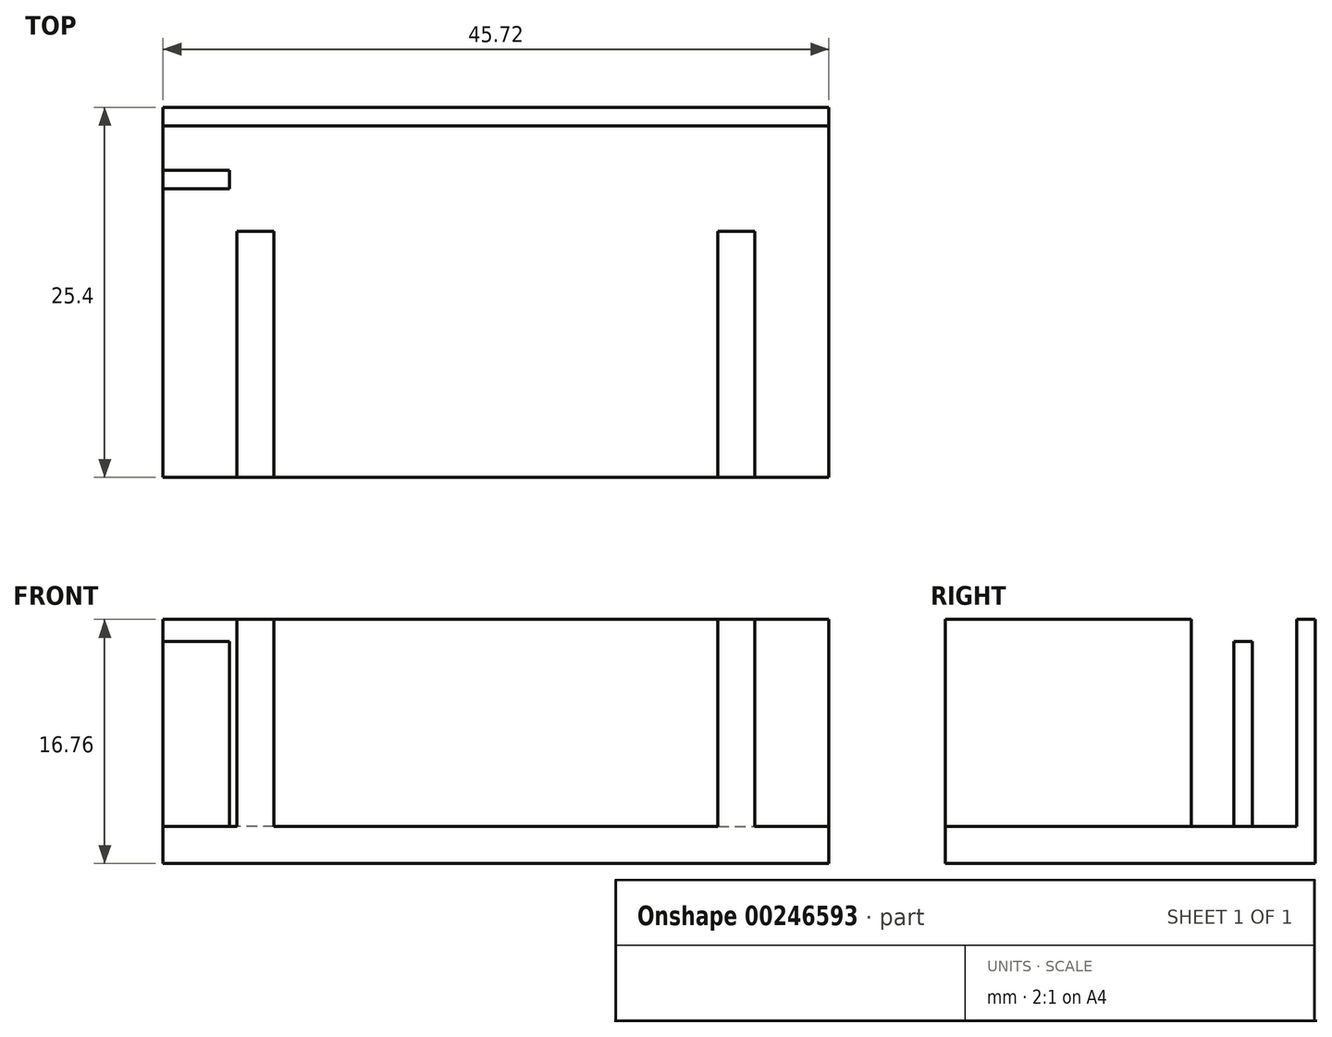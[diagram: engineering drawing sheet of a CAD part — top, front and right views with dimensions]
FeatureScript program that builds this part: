
annotation { "Feature Type Name" : "Feature", "Feature Type Description" : "" }
export const myFeature = defineFeature(function(context is Context, id is Id, definition is map)
    precondition{}
    {
        {
            var Q0;
            Q0=qCreatedBy(makeId("Top.planeOp"),FACE);
            var sketch = newSketch(context, id + "F0", { "sketchPlane" : qUnion([Q0])});
            skLineSegment(sketch, "E0.bottom", {"start": v(-8.43, 7.87) * mm, "end": v(37.3, 7.87) * mm});
            skLineSegment(sketch, "E0.top", {"start": v(-8.43, -17.53) * mm, "end": v(37.3, -17.53) * mm});
            skLineSegment(sketch, "E0.left", {"start": v(-8.43, 7.87) * mm, "end": v(-8.43, -17.53) * mm});
            skLineSegment(sketch, "E0.right", {"start": v(37.3, 7.87) * mm, "end": v(37.3, -17.53) * mm});
            skSolve(sketch);
        }
        {
            var Q0;
            Q0=makeQuery(id+"F0.imprint","IMPRINT",FACE,{"disambiguationData":[TD([[makeQuery(id+"F0.imprint","IMPRINT",EDGE,{"derivedFrom":sQuery(id+"F0.wireOp",EDGE,"E0.bottom")}),-1.0]])]});
            extrude(context, id + "F1", {"entities" : qUnion([Q0]), "depth" : 2.54 * mm});
        }
        {
            var Q0;
            Q0=makeQuery(id+"F1.opExtrude","CAP_FACE",FACE,{"disambiguationData":[OSD([sQuery(id+"F0.wireOp",EDGE,"E0.bottom"),sQuery(id+"F0.wireOp",EDGE,"E0.top"),sQuery(id+"F0.wireOp",EDGE,"E0.left"),sQuery(id+"F0.wireOp",EDGE,"E0.right")])],"isStart":false});
            var sketch = newSketch(context, id + "F2", { "sketchPlane" : qUnion([Q0])});
            skLineSegment(sketch, "E1.bottom", {"start": v(14.43, -17.53) * mm, "end": v(29.67, -17.53) * mm});
            skLineSegment(sketch, "E1.top", {"start": v(14.43, -0.64) * mm, "end": v(29.67, -0.64) * mm});
            skLineSegment(sketch, "E1.left", {"start": v(14.43, -17.53) * mm, "end": v(14.43, -0.64) * mm});
            skLineSegment(sketch, "E1.right", {"start": v(29.67, -17.53) * mm, "end": v(29.67, -0.64) * mm});
            skLineSegment(sketch, "E2.bottom", {"start": v(14.43, -17.53) * mm, "end": v(-0.8, -17.53) * mm});
            skLineSegment(sketch, "E2.top", {"start": v(14.43, -0.64) * mm, "end": v(-0.8, -0.64) * mm});
            skLineSegment(sketch, "E2.right", {"start": v(-0.8, -17.53) * mm, "end": v(-0.8, -0.64) * mm});
            skLineSegment(sketch, "E3.bottom", {"start": v(-0.8, -17.53) * mm, "end": v(-3.35, -17.53) * mm});
            skLineSegment(sketch, "E3.top", {"start": v(-0.8, -0.64) * mm, "end": v(-3.35, -0.64) * mm});
            skLineSegment(sketch, "E3.right", {"start": v(-3.35, -17.53) * mm, "end": v(-3.35, -0.64) * mm});
            skLineSegment(sketch, "E4.bottom", {"start": v(29.67, -17.53) * mm, "end": v(32.21, -17.53) * mm});
            skLineSegment(sketch, "E4.top", {"start": v(29.67, -0.64) * mm, "end": v(32.21, -0.64) * mm});
            skLineSegment(sketch, "E4.right", {"start": v(32.21, -17.53) * mm, "end": v(32.21, -0.64) * mm});
            skSolve(sketch);
        }
        {
            var Q0;
            Q0=makeQuery(id+"F2.imprint","IMPRINT",FACE,{"disambiguationData":[TD([[makeQuery(id+"F2.imprint","IMPRINT",EDGE,{"derivedFrom":sQuery(id+"F2.wireOp",EDGE,"E3.bottom")}),1.0]])]});
            var Q1;
            Q1=makeQuery(id+"F2.imprint","IMPRINT",FACE,{"disambiguationData":[TD([[makeQuery(id+"F2.imprint","IMPRINT",EDGE,{"derivedFrom":sQuery(id+"F2.wireOp",EDGE,"E4.bottom")}),1.0]])]});
            extrude(context, id + "F3", {"entities" : qUnion([Q0, Q1]), "operationType" : NewBodyOperationType.ADD, "depth" : 14.22 * mm});
        }
        {
            var Q0;
            Q0=makeQuery(id+"F1.opExtrude","CAP_FACE",FACE,{"disambiguationData":[OSD([sQuery(id+"F0.wireOp",EDGE,"E0.bottom"),sQuery(id+"F0.wireOp",EDGE,"E0.top"),sQuery(id+"F0.wireOp",EDGE,"E0.left"),sQuery(id+"F0.wireOp",EDGE,"E0.right")])],"isStart":false});
            var sketch = newSketch(context, id + "F4", { "sketchPlane" : qUnion([Q0])});
            skLineSegment(sketch, "E5.bottom", {"start": v(-8.43, 7.87) * mm, "end": v(37.3, 7.87) * mm});
            skLineSegment(sketch, "E5.top", {"start": v(-8.43, 6.6) * mm, "end": v(37.3, 6.6) * mm});
            skLineSegment(sketch, "E5.left", {"start": v(-8.43, 7.87) * mm, "end": v(-8.43, 6.6) * mm});
            skLineSegment(sketch, "E5.right", {"start": v(37.3, 7.87) * mm, "end": v(37.3, 6.6) * mm});
            skSolve(sketch);
        }
        {
            var Q0;
            Q0=makeQuery(id+"F4.imprint","IMPRINT",FACE,{"disambiguationData":[TD([[makeQuery(id+"F4.imprint","IMPRINT",EDGE,{"derivedFrom":sQuery(id+"F4.wireOp",EDGE,"E5.bottom")}),-1.0]])]});
            extrude(context, id + "F5", {"entities" : qUnion([Q0]), "operationType" : NewBodyOperationType.ADD, "depth" : 14.22 * mm});
        }
        {
            var Q0;
            Q0=makeQuery(id+"F1.opExtrude","CAP_FACE",FACE,{"disambiguationData":[OSD([sQuery(id+"F0.wireOp",EDGE,"E0.bottom"),sQuery(id+"F0.wireOp",EDGE,"E0.top"),sQuery(id+"F0.wireOp",EDGE,"E0.left"),sQuery(id+"F0.wireOp",EDGE,"E0.right")])],"isStart":false});
            var sketch = newSketch(context, id + "F6", { "sketchPlane" : qUnion([Q0])});
            skLineSegment(sketch, "E6.bottom", {"start": v(-8.43, 6.6) * mm, "end": v(-3.85, 6.6) * mm});
            skLineSegment(sketch, "E6.top", {"start": v(-8.43, 3.55) * mm, "end": v(-3.85, 3.55) * mm});
            skLineSegment(sketch, "E6.left", {"start": v(-8.43, 6.6) * mm, "end": v(-8.43, 3.55) * mm});
            skLineSegment(sketch, "E6.right", {"start": v(-3.85, 6.6) * mm, "end": v(-3.85, 3.55) * mm});
            skLineSegment(sketch, "E7.bottom", {"start": v(37.3, 6.6) * mm, "end": v(32.72, 6.6) * mm});
            skLineSegment(sketch, "E7.top", {"start": v(37.3, 3.55) * mm, "end": v(32.72, 3.55) * mm});
            skLineSegment(sketch, "E7.left", {"start": v(37.3, 6.6) * mm, "end": v(37.3, 3.55) * mm});
            skLineSegment(sketch, "E7.right", {"start": v(32.72, 6.6) * mm, "end": v(32.72, 3.55) * mm});
            skLineSegment(sketch, "E8.top", {"start": v(-8.43, 2.28) * mm, "end": v(-3.85, 2.28) * mm});
            skLineSegment(sketch, "E8.left", {"start": v(-8.43, 3.55) * mm, "end": v(-8.43, 2.28) * mm});
            skLineSegment(sketch, "E8.right", {"start": v(-3.85, 3.55) * mm, "end": v(-3.85, 2.28) * mm});
            skLineSegment(sketch, "E9.top", {"start": v(37.3, 2.28) * mm, "end": v(32.72, 2.28) * mm});
            skLineSegment(sketch, "E9.left", {"start": v(37.3, 3.55) * mm, "end": v(37.3, 2.28) * mm});
            skLineSegment(sketch, "E9.right", {"start": v(32.72, 3.55) * mm, "end": v(32.72, 2.28) * mm});
            skSolve(sketch);
        }
        {
            var Q0;
            Q0=makeQuery(id+"F6.imprint","IMPRINT",FACE,{"disambiguationData":[TD([[makeQuery(id+"F6.imprint","IMPRINT",EDGE,{"derivedFrom":sQuery(id+"F6.wireOp",EDGE,"E6.top")}),-1.0]])]});
            var Q1;
            Q1=makeQuery(id+"F6.imprint","IMPRINT",FACE,{"disambiguationData":[TD([[makeQuery(id+"F6.imprint","IMPRINT",EDGE,{"derivedFrom":sQuery(id+"F6.wireOp",EDGE,"E7.top")}),1.0]])]});
            extrude(context, id + "F7", {"entities" : qUnion([Q0, Q1]), "operationType" : NewBodyOperationType.ADD, "depth" : 12.7 * mm});
        }
    });
